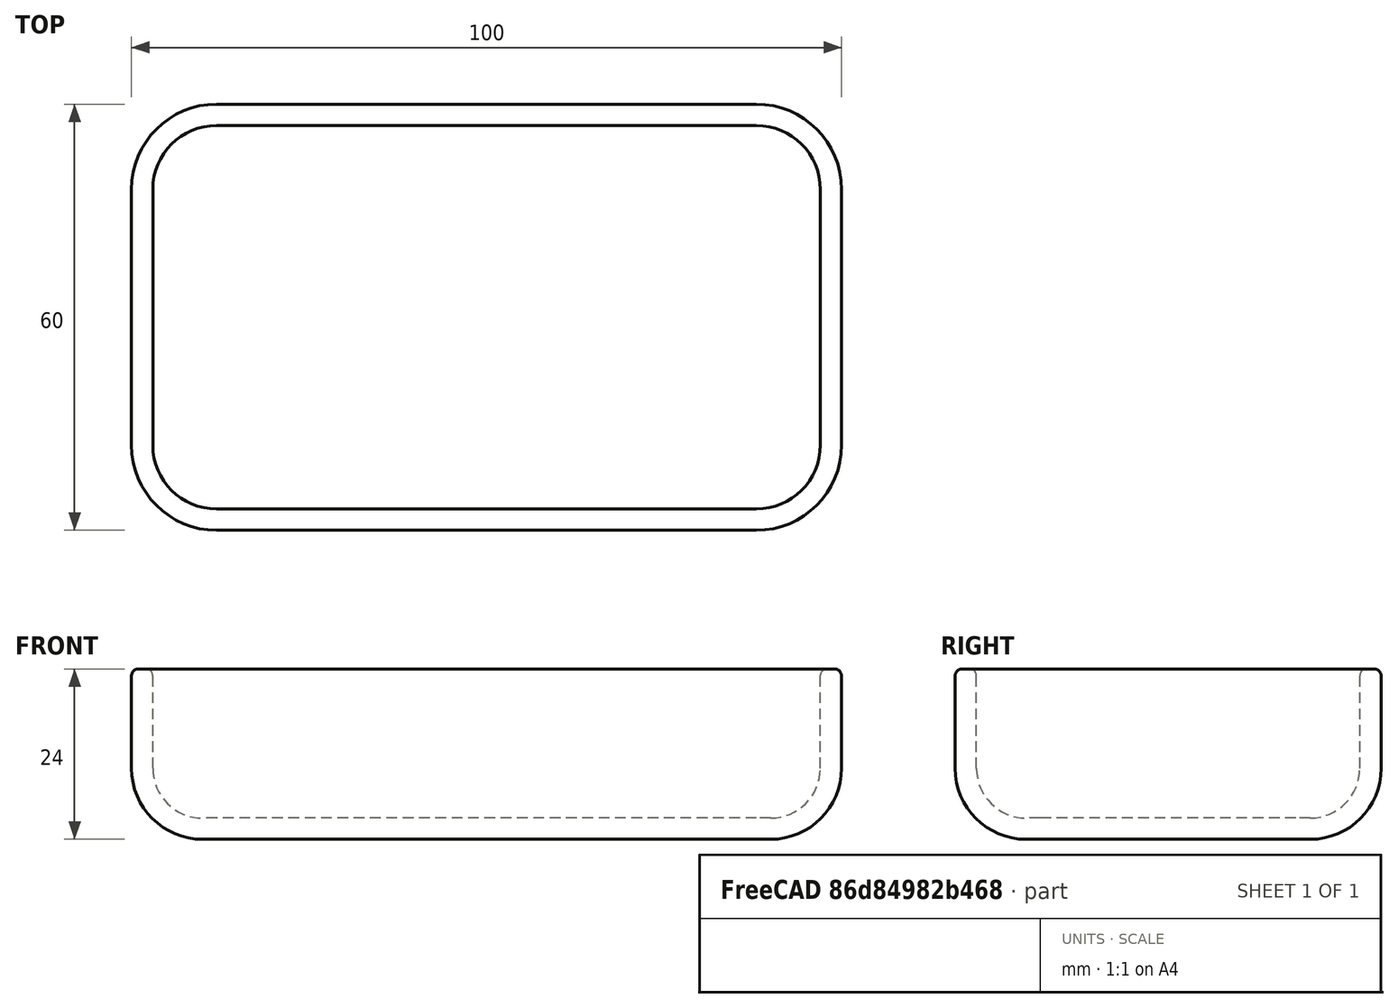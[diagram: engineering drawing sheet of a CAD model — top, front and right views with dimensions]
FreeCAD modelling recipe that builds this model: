
FCSTD DOCUMENT  (FreeCAD 1.1R20251125 (Git shallow))
Label: Posodica
License: All rights reserved
LicenseURL: https://en.wikipedia.org/wiki/All_rights_reserved
objects: TechDraw::DrawViewDimension×9, PartDesign::Fillet×2, TechDraw::DrawSVGTemplate×1, Sketcher::SketchObject×1, PartDesign::Pad×1, PartDesign::Thickness×1, PartDesign::Body×1, TechDraw::DrawViewImage×1, App::Point×1, TechDraw::DrawProjGroupItem×1, TechDraw::DrawViewSection×1, TechDraw::DrawViewDetail×1, TechDraw::DrawViewAnnotation×1, TechDraw::DrawHatch×1, TechDraw::DrawPage×1
note: 28 computed .brp shape members not serialized (recipe doc carries the construction recipe); baked Part::Feature solids carry a one-line shape summary decoded from their .brp

FEATURE [TechDraw::DrawSVGTemplate] Template
  EditableTexts = NazivRisbe=Posodica; a3=A4; ime_avtorja=dr. David Rihtaršič; masaizd=? g; mateial=PETG (1380 kg/m3); merilo=1 : 1
  Height = 210
  Orientation = 1
  Template = <userpath>/Files/Work/UL-PeF/Vaje/Tehnicna_dokumentacija/FreeCAD_PeF_Glava/FreeCadGlave/A4_Land_PeF_DWD_DR.svg
  Width = 297
FEATURE [Sketcher::SketchObject] Sketch
  ArcFitTolerance = 1e-06
  AttachmentSupport = -> [Origin]
  ExternalTypes = [0]
  FullyConstrained = true
  MakeInternals = false
  MapMode = 5
  sketch-geometry (10):
    g0: LineSegment StartX=-38 StartY=-30 StartZ=0 EndX=38 EndY=-30 EndZ=0
    g1: LineSegment StartX=50 StartY=-18 StartZ=0 EndX=50 EndY=18 EndZ=0
    g2: LineSegment StartX=38 StartY=30 StartZ=0 EndX=-38 EndY=30 EndZ=0
    g3: LineSegment StartX=-50 StartY=18 StartZ=0 EndX=-50 EndY=-18 EndZ=0
    g4: ArcOfCircle CenterX=-38 CenterY=-18 CenterZ=0 NormalX=0 NormalY=0 NormalZ=1 AngleXU=0 Radius=12 StartAngle=3.14159 EndAngle=4.71239
    g5: ArcOfCircle CenterX=38 CenterY=-18 CenterZ=0 NormalX=0 NormalY=0 NormalZ=1 AngleXU=0 Radius=12 StartAngle=4.71239 EndAngle=6.28319
    g6: ArcOfCircle CenterX=38 CenterY=18 CenterZ=0 NormalX=0 NormalY=0 NormalZ=1 AngleXU=0 Radius=12 StartAngle=0 EndAngle=1.5708
    g7: ArcOfCircle CenterX=-38 CenterY=18 CenterZ=0 NormalX=0 NormalY=0 NormalZ=1 AngleXU=0 Radius=12 StartAngle=1.5708 EndAngle=3.14159
    g8: GeomPoint [constr] X=50 Y=30 Z=0
    g9: GeomPoint [constr] X=4.2e-15 Y=-3.4e-15 Z=0
  constraints (22):
    c: Tangent(g0,g4) = -1.5708
    c: Tangent(g0,g5) = -1.5708
    c: Tangent(g1,g5) = -1.5708
    c: Tangent(g1,g6) = -1.5708
    c: Tangent(g2,g6) = -1.5708
    c: Tangent(g2,g7) = -1.5708
    c: Tangent(g3,g7) = -1.5708
    c: Tangent(g3,g4) = -1.5708
    c: Horizontal(g0)
    c: Horizontal(g2)
    c: Vertical(g1)
    c: Vertical(g3)
    c: Equal(g4,g5)
    c: Equal(g5,g6)
    c: Equal(g6,g7)
    c: Symmetric(g2,g0,g9)
    c: PointOnObject(g8,g1)
    c: PointOnObject(g8,g2)
    c: Distance(g1,g3) = 100
    c: Distance(g0,g2) = 60
    c: Radius(g5) = 12
    c: Coincident(g9,g-1)
FEATURE [PartDesign::Pad] Pad
  Direction = (0,0,1)
  Length = 24
  Length2 = 10
  Profile = -> Sketch
  ReferenceAxis = -> Sketch [N_Axis]
  Refine = true
  SideType = 0
  Suppressed = false
  Type = 0
  Type2 = 0
FEATURE [PartDesign::Fillet] Fillet
  Base = -> Pad [Edge3]
  BaseFeature = -> Pad
  Radius = 10
  Refine = true
  SupportTransform = false
  Suppressed = false
  UseAllEdges = false
FEATURE [PartDesign::Thickness] Thickness
  Base = -> Fillet [Face4]
  BaseFeature = -> Fillet
  Intersection = false
  Join = 0
  Mode = 0
  Refine = true
  Reversed = true
  SupportTransform = false
  Suppressed = false
  Value = 3
FEATURE [PartDesign::Fillet] Fillet001
  Base = -> Thickness [Edge3,Edge43]
  BaseFeature = -> Thickness
  Radius = 1
  Refine = true
  SupportTransform = false
  Suppressed = false
  UseAllEdges = false
FEATURE [PartDesign::Body] Body  label="Posodica"
  AllowCompound = false
  Group = -> [Sketch,Pad,Fillet,Thickness,Fillet001]
  Origin = -> Origin
  Tip = -> Fillet001
FEATURE [TechDraw::DrawViewImage] ActiveView
  Height = 102.4
  ImageFile = <userpath>/.cache/FreeCAD/Cache/FreeCAD_Doc_48bb8346-4335-484d-920e-0e4550ab23fa_28d1b8_497435/PageActiveViewbEeZCr.png
  LockPosition = false
  Rotation = 0
  ScaleType = 2
  Width = 128
  X = 226.488
  Y = 72.5756
FEATURE [App::Point] Origin001  label="Origin"
  Role = Origin
FEATURE [TechDraw::DrawProjGroupItem] View
  CoarseView = false
  Direction = (0,0,1)
  Focus = 100
  HardHidden = true
  IsoCount = 0
  IsoHidden = false
  IsoVisible = false
  LockPosition = false
  Perspective = false
  Rotation = 0
  RotationVector = (1,0,0)
  ScaleType = 0
  ScrubCount = 1
  SeamHidden = false
  SeamVisible = false
  SmoothHidden = false
  SmoothVisible = false
  Source = -> [Fillet001]
  Type = 0
  X = 91.6412
  XDirection = (1,0,0)
  Y = 92.7947
FEATURE [TechDraw::DrawViewSection] SectionView  label="Section A - A"
  BaseView = -> View
  CoarseView = false
  CutSurfaceDisplay = 2
  Direction = (1e-16,-1,0)
  FileGeomPattern = <path>
  FileHatchPattern = <path>
  Focus = 100
  FuseBeforeCut = false
  HardHidden = true
  HatchOffset = (0,0,0)
  HatchRotation = 0
  HatchScale = 1
  IsoCount = 0
  IsoHidden = false
  IsoVisible = false
  LockPosition = false
  NameGeomPattern = Diamond
  Perspective = false
  Rotation = 0
  ScaleType = 0
  ScrubCount = 1
  SeamHidden = false
  SeamVisible = false
  SectionDirection = 4
  SectionLineStretch = 1
  SectionNormal = (1e-16,-1,0)
  SectionOrigin = (0,0,12)
  SectionSymbol = A
  SmoothHidden = false
  SmoothVisible = false
  Source = -> [Fillet001]
  TrimAfterCut = false
  UsePreviousCut = false
  X = 91.6412
  XDirection = (1,1e-16,0)
  Y = 153.078
FEATURE [TechDraw::DrawViewDimension] Dimension
  AngleOverride = false
  Arbitrary = false
  ArbitraryTolerances = false
  BoxCorners = (2) [(-50,-30,0),(50,30,0)]
  EqualTolerance = true
  ExtensionAngle = 0
  FormatSpec = %.2w
  FormatSpecOverTolerance = %+.2w
  FormatSpecUnderTolerance = %+.2w
  Inverted = false
  LineAngle = 0
  LockPosition = false
  MeasureType = 1
  OverTolerance = 0
  References2D = -> [View]
  Rotation = 0
  ScaleType = 0
  ShowUnits = false
  TheoreticalExact = false
  Type = 0
  UnderTolerance = 0
  UseActualArea = true
  X = 0
  Y = -36.75
FEATURE [TechDraw::DrawViewDimension] Dimension001
  AngleOverride = false
  Arbitrary = false
  ArbitraryTolerances = false
  BoxCorners = (2) [(-50,-30,0),(50,30,0)]
  EqualTolerance = true
  ExtensionAngle = 0
  FormatSpec = %.2w
  FormatSpecOverTolerance = %+.2w
  FormatSpecUnderTolerance = %+.2w
  Inverted = false
  LineAngle = 0
  LockPosition = false
  MeasureType = 1
  OverTolerance = 0
  References2D = -> [View]
  Rotation = 0
  ScaleType = 0
  ShowUnits = false
  TheoreticalExact = false
  Type = 0
  UnderTolerance = 0
  UseActualArea = true
  X = -63.41
  Y = 0
FEATURE [TechDraw::DrawViewDimension] Dimension002
  AngleOverride = false
  Arbitrary = false
  ArbitraryTolerances = false
  BoxCorners = (2) [(-50,-30,0),(50,30,0)]
  EqualTolerance = true
  ExtensionAngle = 0
  FormatSpec = R%.2w
  FormatSpecOverTolerance = %+.2w
  FormatSpecUnderTolerance = %+.2w
  Inverted = false
  LineAngle = 0
  LockPosition = false
  MeasureType = 1
  OverTolerance = 0
  References2D = -> [View]
  Rotation = 0
  ScaleType = 0
  ShowUnits = false
  TheoreticalExact = false
  Type = 4
  UnderTolerance = 0
  UseActualArea = true
  X = 54.2408
  Y = 31.4981
FEATURE [TechDraw::DrawViewDimension] Dimension003
  AngleOverride = false
  Arbitrary = false
  ArbitraryTolerances = false
  BoxCorners = (2) [(-50,-30,0),(50,30,0)]
  EqualTolerance = true
  ExtensionAngle = 0
  FormatSpec = R%.2w
  FormatSpecOverTolerance = %+.2w
  FormatSpecUnderTolerance = %+.2w
  Inverted = false
  LineAngle = 0
  LockPosition = false
  MeasureType = 1
  OverTolerance = 0
  References2D = -> [View]
  Rotation = 0
  ScaleType = 0
  ShowUnits = false
  TheoreticalExact = false
  Type = 4
  UnderTolerance = 0
  UseActualArea = true
  X = 36.0399
  Y = -13.6641
FEATURE [TechDraw::DrawViewDimension] Dimension004
  AngleOverride = false
  Arbitrary = false
  ArbitraryTolerances = false
  BoxCorners = (2) [(-50,-30,0),(50,30,0)]
  EqualTolerance = true
  ExtensionAngle = 0
  FormatSpec = %.2w
  FormatSpecOverTolerance = %+.2w
  FormatSpecUnderTolerance = %+.2w
  Inverted = false
  LineAngle = 0
  LockPosition = false
  MeasureType = 1
  OverTolerance = 0
  References2D = -> [View]
  Rotation = 0
  ScaleType = 0
  ShowUnits = false
  TheoreticalExact = false
  Type = 0
  UnderTolerance = 0
  UseActualArea = true
  X = 30.9349
  Y = 37.9285
FEATURE [TechDraw::DrawViewDimension] Dimension005
  AngleOverride = false
  Arbitrary = false
  ArbitraryTolerances = false
  BoxCorners = (2) [(-50,-12,-1e-07),(50,12,1e-07)]
  EqualTolerance = true
  ExtensionAngle = 0
  FormatSpec = %.2w
  FormatSpecOverTolerance = %+.2w
  FormatSpecUnderTolerance = %+.2w
  Inverted = false
  LineAngle = 0
  LockPosition = false
  MeasureType = 1
  OverTolerance = 0
  References2D = -> [SectionView]
  Rotation = 0
  ScaleType = 0
  ShowUnits = false
  TheoreticalExact = false
  Type = 0
  UnderTolerance = 0
  UseActualArea = true
  X = -63.34
  Y = 0
FEATURE [TechDraw::DrawViewDimension] Dimension006
  AngleOverride = false
  Arbitrary = false
  ArbitraryTolerances = false
  BoxCorners = (2) [(-50,-12,-1e-07),(50,12,1e-07)]
  EqualTolerance = true
  ExtensionAngle = 0
  FormatSpec = R%.2w
  FormatSpecOverTolerance = %+.2w
  FormatSpecUnderTolerance = %+.2w
  Inverted = false
  LineAngle = 0
  LockPosition = false
  MeasureType = 1
  OverTolerance = 0
  References2D = -> [SectionView]
  Rotation = 0
  ScaleType = 0
  ShowUnits = false
  TheoreticalExact = false
  Type = 4
  UnderTolerance = 0
  UseActualArea = true
  X = -38.5487
  Y = 3.44747
FEATURE [TechDraw::DrawViewDimension] Dimension007
  AngleOverride = false
  Arbitrary = false
  ArbitraryTolerances = false
  BoxCorners = (2) [(-50,-12,-1e-07),(50,12,1e-07)]
  EqualTolerance = true
  ExtensionAngle = 0
  FormatSpec = R%.2w
  FormatSpecOverTolerance = %+.2w
  FormatSpecUnderTolerance = %+.2w
  Inverted = false
  LineAngle = 0
  LockPosition = false
  MeasureType = 1
  OverTolerance = 0
  References2D = -> [SectionView]
  Rotation = 0
  ScaleType = 0
  ShowUnits = false
  TheoreticalExact = false
  Type = 4
  UnderTolerance = 0
  UseActualArea = true
  X = 57.4313
  Y = -10.4913
FEATURE [TechDraw::DrawViewDetail] Detail
  AnchorPoint = (49,12,0)
  BaseView = -> SectionView
  CoarseView = false
  Direction = (1e-16,-1,0)
  Focus = 100
  HardHidden = true
  IsoCount = 0
  IsoHidden = false
  IsoVisible = false
  LockPosition = false
  Perspective = false
  Radius = 7
  Reference = 1
  Rotation = 0
  Scale = 5
  ScaleType = 2
  ScrubCount = 1
  SeamHidden = false
  SeamVisible = false
  ShowHighlight = true
  ShowMatting = true
  SmoothHidden = false
  SmoothVisible = false
  Source = -> [Fillet001]
  X = 214.05
  XDirection = (1,1e-16,0)
  Y = 153.078
FEATURE [TechDraw::DrawViewAnnotation] Annotation
  Font = ISOCPEUR
  LineSpace = 100
  LockPosition = false
  MaxWidth = -1
  Rotation = 0
  ScaleType = 0
  Text = M 5:1
  TextSize = 3.5
  TextStyle = 0
  X = 246.967
  Y = 185.069
FEATURE [TechDraw::DrawHatch] Hatch
  HatchPattern = <path>
  Source = -> Detail [Face2]
FEATURE [TechDraw::DrawViewDimension] Dimension008
  AngleOverride = false
  Arbitrary = false
  ArbitraryTolerances = false
  BoxCorners = (2) [(-35.35,-1e-07,-1e-07),(5,35.35,1e-07)]
  EqualTolerance = true
  ExtensionAngle = 0
  FormatSpec = 2× R%.2w
  FormatSpecOverTolerance = %+.2w
  FormatSpecUnderTolerance = %+.2w
  Inverted = false
  LineAngle = 0
  LockPosition = false
  MeasureType = 1
  OverTolerance = 0
  References2D = -> [Detail]
  Rotation = 0
  ScaleType = 0
  ShowUnits = false
  TheoreticalExact = false
  Type = 4
  UnderTolerance = 0
  UseActualArea = true
  X = 14.0083
  Y = 8.22802
FEATURE [TechDraw::DrawPage] Page
  KeepUpdated = true
  NextBalloonIndex = 1
  ProjectionType = 0
  Template = -> Template
  Views = -> [ActiveView,View,SectionView,Dimension,Dimension001,Dimension002,Dimension003,Dimension004,Dimension005,Dimension006,Dimension007,Detail,Annotation,Dimension008]
note: 3 file-system paths scrubbed to <path> (originals preserved in the JSON sidecar)
